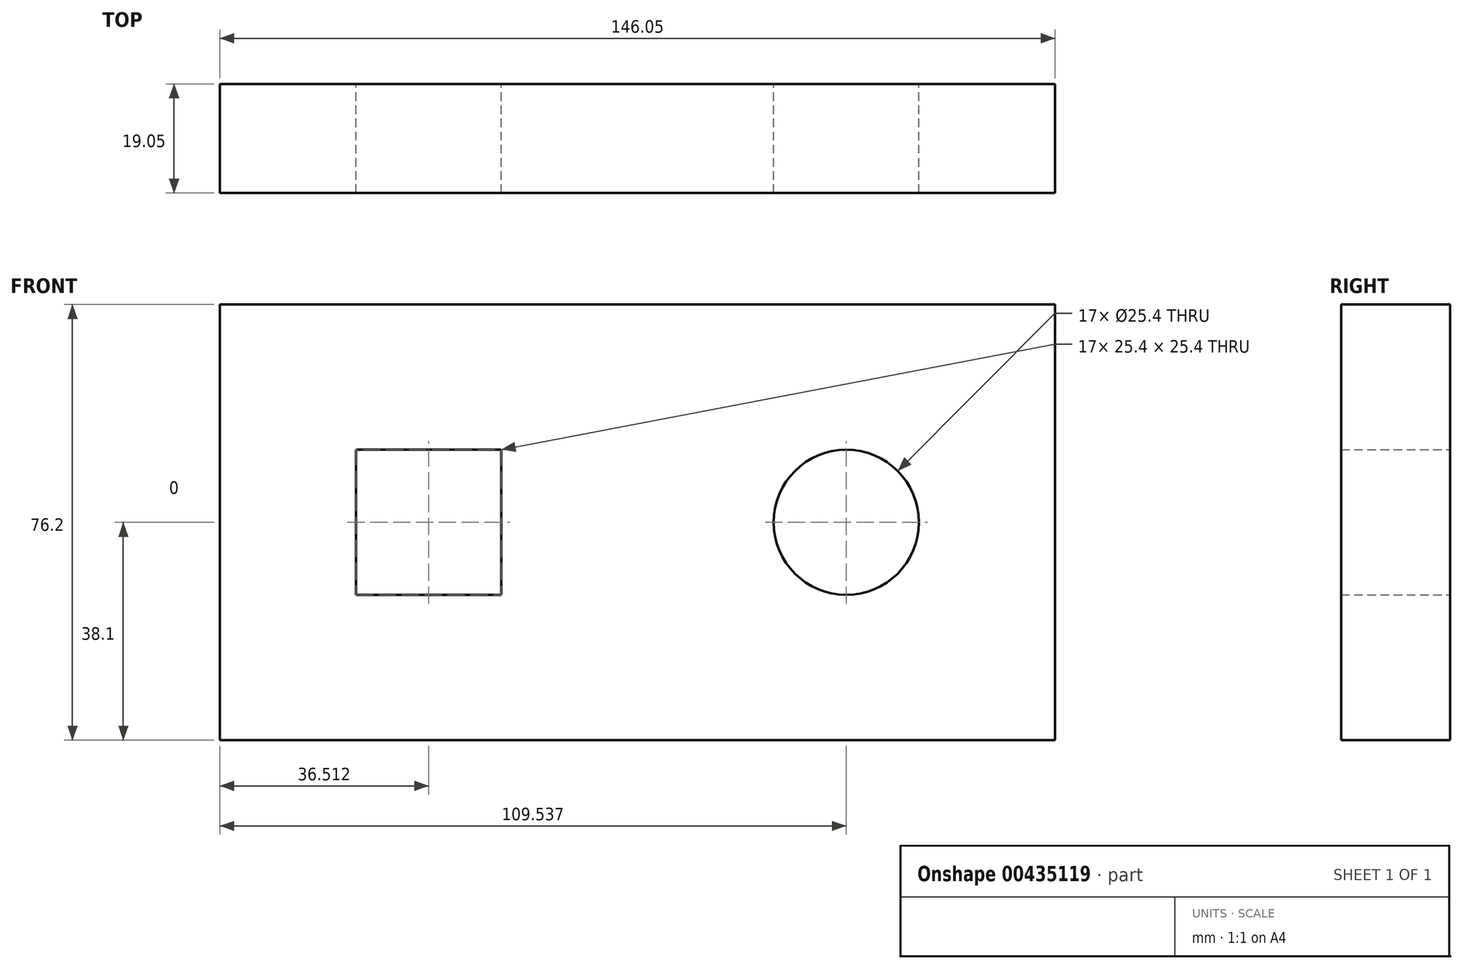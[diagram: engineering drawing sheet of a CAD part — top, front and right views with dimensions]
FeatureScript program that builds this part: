
annotation { "Feature Type Name" : "Feature", "Feature Type Description" : "" }
export const myFeature = defineFeature(function(context is Context, id is Id, definition is map)
    precondition{}
    {
        {
            var Q0;
            Q0=qCreatedBy(makeId("Front.planeOp"),FACE);
            var sketch = newSketch(context, id + "F0", { "sketchPlane" : qUnion([Q0])});
            skLineSegment(sketch, "E0.bottom", {"start": v(-59.1, 76.2) * mm, "end": v(86.95, 76.2) * mm});
            skLineSegment(sketch, "E0.top", {"start": v(-59.1, 0) * mm, "end": v(86.95, 0) * mm});
            skLineSegment(sketch, "E0.left", {"start": v(-59.1, 76.2) * mm, "end": v(-59.1, 0) * mm});
            skLineSegment(sketch, "E0.right", {"start": v(86.95, 76.2) * mm, "end": v(86.95, 0) * mm});
            skLineSegment(sketch, "E1.bottom", {"start": v(-35.29, 50.8) * mm, "end": v(-9.89, 50.8) * mm});
            skLineSegment(sketch, "E1.top", {"start": v(-35.29, 25.4) * mm, "end": v(-9.89, 25.4) * mm});
            skLineSegment(sketch, "E1.left", {"start": v(-35.29, 50.8) * mm, "end": v(-35.29, 25.4) * mm});
            skLineSegment(sketch, "E1.right", {"start": v(-9.89, 50.8) * mm, "end": v(-9.89, 25.4) * mm});
            skCircle(sketch, "E2", {"center": v(50.44, 38.1) * mm, "radius": 12.7 * mm});
            skSolve(sketch);
        }
        {
            var Q0;
            Q0 = qSketchRegion(id + "F0", true);
            extrude(context, id + "F1", {"entities" : qUnion([Q0]), "depth" : 19.05 * mm});
        }
    });
